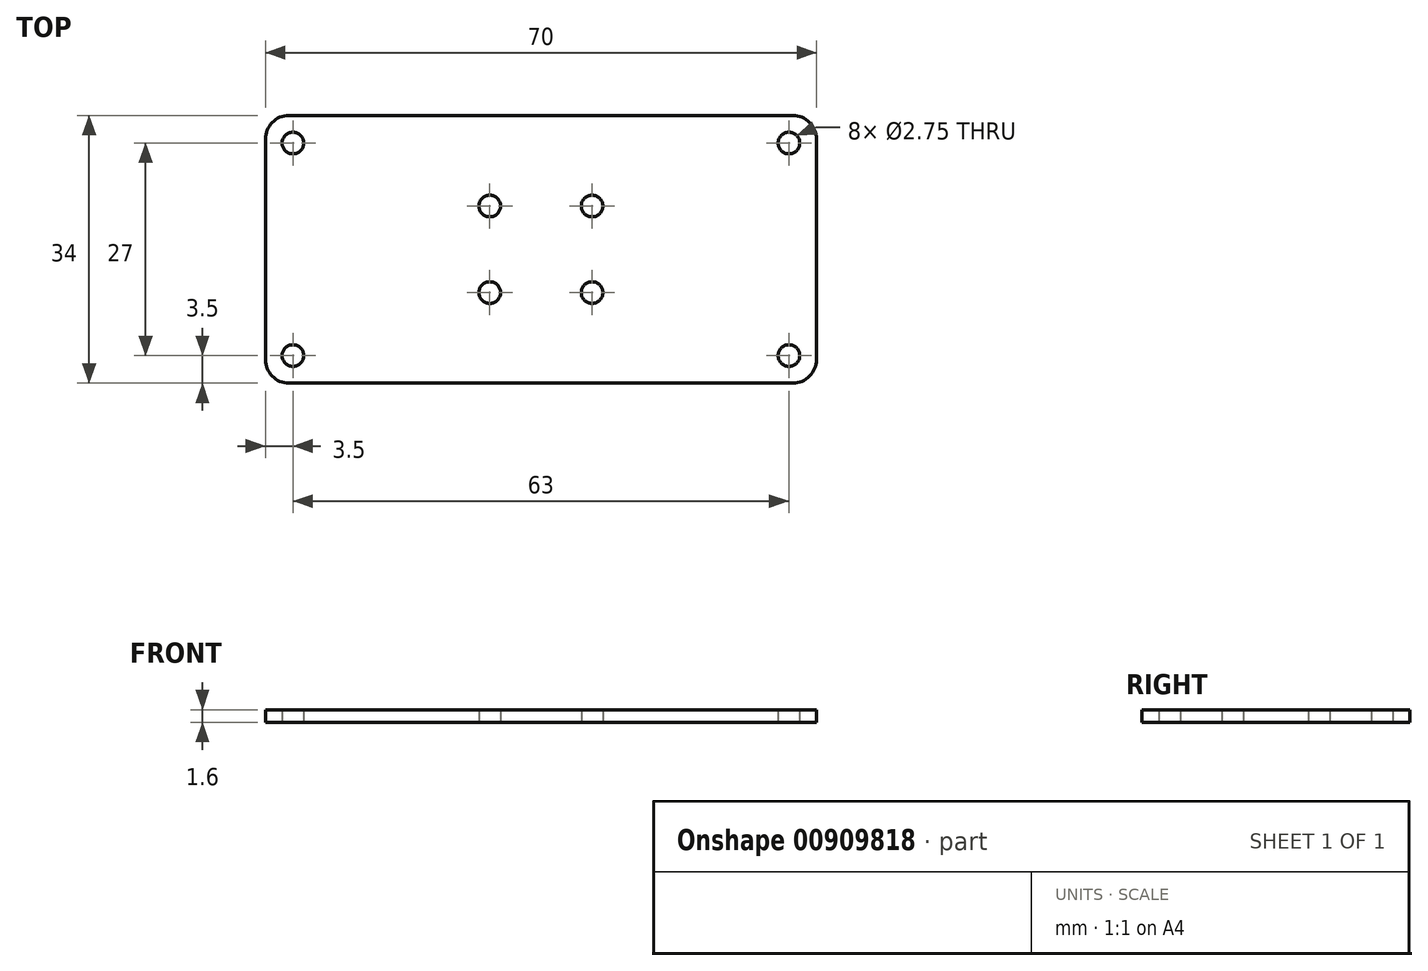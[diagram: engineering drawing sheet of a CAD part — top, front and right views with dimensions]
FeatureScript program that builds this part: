
annotation { "Feature Type Name" : "Feature", "Feature Type Description" : "" }
export const myFeature = defineFeature(function(context is Context, id is Id, definition is map)
    precondition{}
    {
        {
            var Q0;
            Q0=qCreatedBy(makeId("Top.planeOp"),FACE);
            var sketch = newSketch(context, id + "F0", { "sketchPlane" : qUnion([Q0])});
            skLineSegment(sketch, "E0.bottom", {"start": v(3, 0) * mm, "end": v(67, 0) * mm});
            skLineSegment(sketch, "E0.top", {"start": v(3, 34) * mm, "end": v(67, 34) * mm});
            skLineSegment(sketch, "E0.left", {"start": v(0, 3) * mm, "end": v(0, 31) * mm});
            skLineSegment(sketch, "E0.right", {"start": v(70, 3) * mm, "end": v(70, 31) * mm});
            skPoint(sketch, "E1.visualSharp", {"position": v(0, 34) * mm});
            skArc(sketch, "E1.filletArc", {"start": v(3, 34) * mm, "mid": v(0.88, 33.12) * mm, "end": v(0, 31) * mm});
            skPoint(sketch, "E2.visualSharp", {"position": v(0, 0) * mm});
            skArc(sketch, "E2.filletArc", {"start": v(0, 3) * mm, "mid": v(0.88, 0.88) * mm, "end": v(3, 0) * mm});
            skPoint(sketch, "E3.visualSharp", {"position": v(70, 0) * mm});
            skArc(sketch, "E3.filletArc", {"start": v(67, 0) * mm, "mid": v(69.12, 0.88) * mm, "end": v(70, 3) * mm});
            skPoint(sketch, "E4.visualSharp", {"position": v(70, 34) * mm});
            skArc(sketch, "E4.filletArc", {"start": v(70, 31) * mm, "mid": v(69.12, 33.12) * mm, "end": v(67, 34) * mm});
            skCircle(sketch, "E5", {"center": v(3.5, 30.5) * mm, "radius": 1.38 * mm});
            skCircle(sketch, "E6", {"center": v(3.5, 3.5) * mm, "radius": 1.38 * mm});
            skCircle(sketch, "E7", {"center": v(66.5, 3.5) * mm, "radius": 1.38 * mm});
            skCircle(sketch, "E8", {"center": v(66.5, 30.5) * mm, "radius": 1.38 * mm});
            skPoint(sketch, "E9.orphan", {"position": v(0, 17) * mm});
            skPoint(sketch, "E10.end.orphan", {"position": v(70, 17) * mm});
            skCircle(sketch, "E11", {"center": v(28.5, 22.5) * mm, "radius": 1.38 * mm});
            skCircle(sketch, "E12", {"center": v(41.5, 22.5) * mm, "radius": 1.38 * mm});
            skCircle(sketch, "E13", {"center": v(41.5, 11.5) * mm, "radius": 1.38 * mm});
            skCircle(sketch, "E14", {"center": v(28.5, 11.5) * mm, "radius": 1.38 * mm});
            skSolve(sketch);
        }
        {
            var Q0;
            Q0 = qSketchRegion(id + "F0", true);
            extrude(context, id + "F1", {"entities" : qUnion([Q0]), "depth" : 1.6 * mm, "offsetDistance" : 25 * mm});
        }
    });
